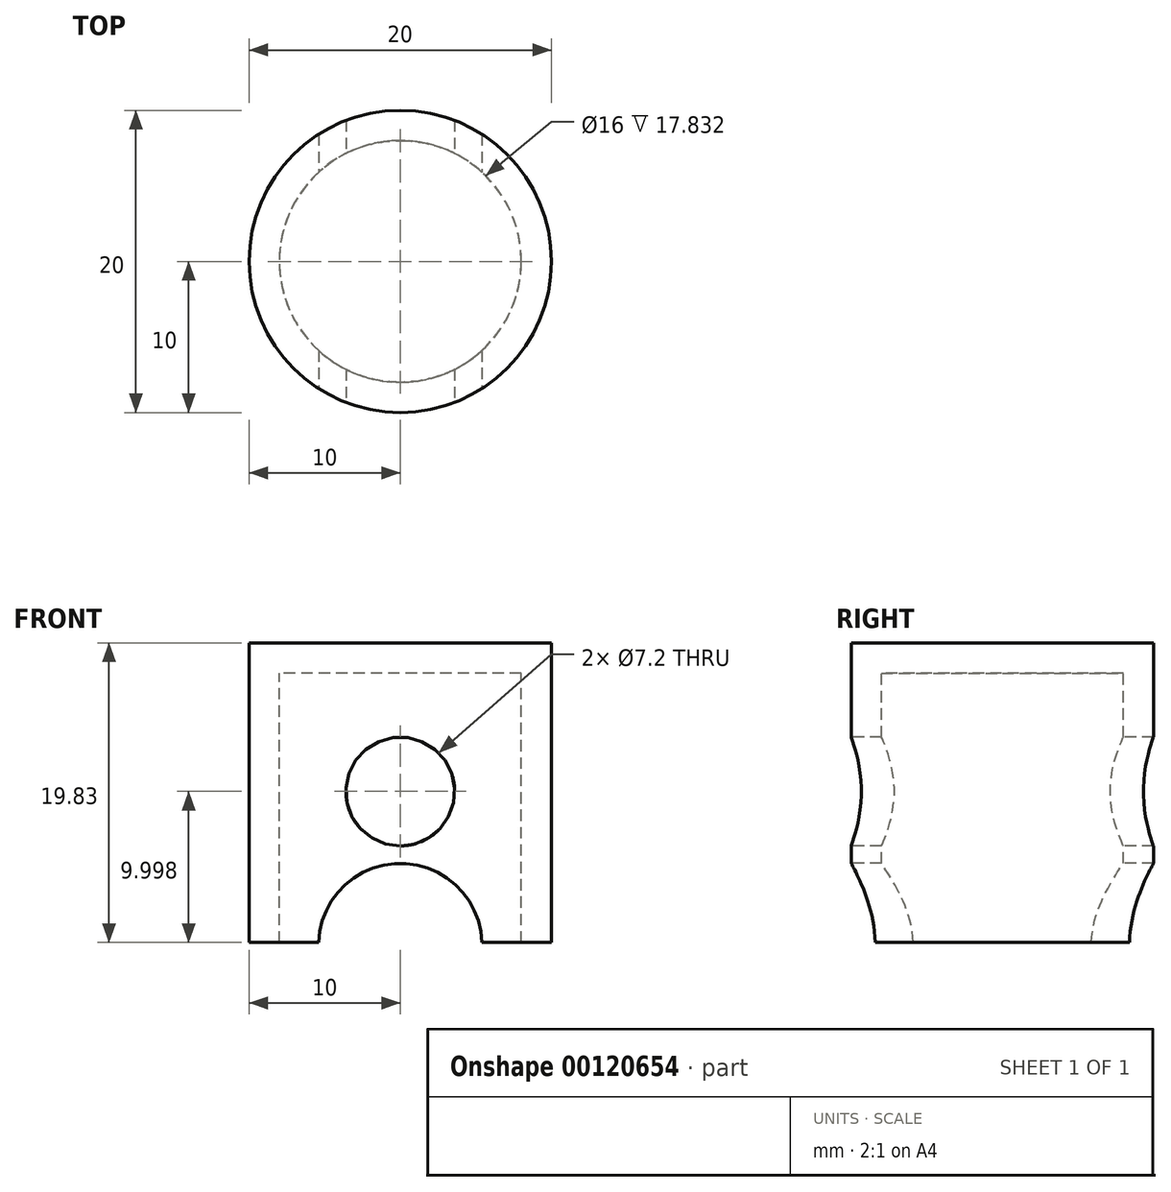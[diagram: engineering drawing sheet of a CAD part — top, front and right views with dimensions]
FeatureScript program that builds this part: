
annotation { "Feature Type Name" : "Feature", "Feature Type Description" : "" }
export const myFeature = defineFeature(function(context is Context, id is Id, definition is map)
    precondition{}
    {
        {
            var Q0;
            Q0=qCreatedBy(makeId("Right.planeOp"),FACE);
            var sketch = newSketch(context, id + "F0", { "sketchPlane" : qUnion([Q0])});
            skLineSegment(sketch, "E0", {"start": v(0, 20) * mm, "end": v(-10, 20) * mm});
            skLineSegment(sketch, "E1", {"start": v(-10, 20) * mm, "end": v(-10, 0) * mm});
            skLineSegment(sketch, "E2", {"start": v(-10.13, 0.17) * mm, "end": v(-7.11, 0.17) * mm});
            skLineSegment(sketch, "E3", {"start": v(-8, 0.03) * mm, "end": v(-8, 18) * mm});
            skLineSegment(sketch, "E4", {"start": v(-8, 18) * mm, "end": v(0, 18) * mm});
            skLineSegment(sketch, "E5", {"start": v(0, 20) * mm, "end": v(0, 18) * mm});
            skSolve(sketch);
        }
        {
            var Q0;
            Q0=qCreatedBy(makeId("Front.planeOp"),FACE);
            var sketch = newSketch(context, id + "F1", { "sketchPlane" : qUnion([Q0])});
            skLineSegment(sketch, "E6", {"start": v(0, 19.87) * mm, "end": v(0, 0) * mm, "construction": true});
            skSolve(sketch);
        }
        {
            var Q0;
            Q0 = qSketchRegion(id + "F0", true);
            var Q1;
            Q1=sQuery(id+"F1.wireOp",EDGE,"E6");
            revolve(context, id + "F2", {"entities" : qUnion([Q0]), "axis" : qUnion([Q1]), "revolveType" : RevolveType.FULL});
        }
        {
            var Q0;
            Q0=qCreatedBy(makeId("Front.planeOp"),FACE);
            var sketch = newSketch(context, id + "F3", { "sketchPlane" : qUnion([Q0])});
            skCircle(sketch, "E7", {"center": v(0, 10.17) * mm, "radius": 3.6 * mm});
            skSolve(sketch);
        }
        {
            var Q0;
            Q0 = qSketchRegion(id + "F3", true);
            extrude(context, id + "F4", {"entities" : qUnion([Q0]), "operationType" : NewBodyOperationType.REMOVE, "endBound" : BoundingType.THROUGH_ALL, "oppositeDirection" : true, "depth" : 25 * mm, "hasSecondDirection" : true, "secondDirectionBound" : SecondDirectionBoundingType.THROUGH_ALL, "secondDirectionOppositeDirection" : false, "secondDirectionDepth" : 25 * mm});
        }
        {
            var Q0;
            Q0=qCreatedBy(makeId("Front.planeOp"),FACE);
            var sketch = newSketch(context, id + "F5", { "sketchPlane" : qUnion([Q0])});
            skArc(sketch, "E8", {"start": v(5.41, 0) * mm, "mid": v(0, 5.41) * mm, "end": v(-5.41, 0) * mm});
            skLineSegment(sketch, "E9", {"start": v(-5.41, 0) * mm, "end": v(5.41, 0) * mm});
            skSolve(sketch);
        }
        {
            var Q0;
            Q0 = qSketchRegion(id + "F5", true);
            extrude(context, id + "F6", {"entities" : qUnion([Q0]), "operationType" : NewBodyOperationType.REMOVE, "endBound" : BoundingType.THROUGH_ALL, "oppositeDirection" : true, "depth" : 25 * mm, "hasSecondDirection" : true, "secondDirectionBound" : SecondDirectionBoundingType.THROUGH_ALL, "secondDirectionOppositeDirection" : false, "secondDirectionDepth" : 25 * mm});
        }
    });
